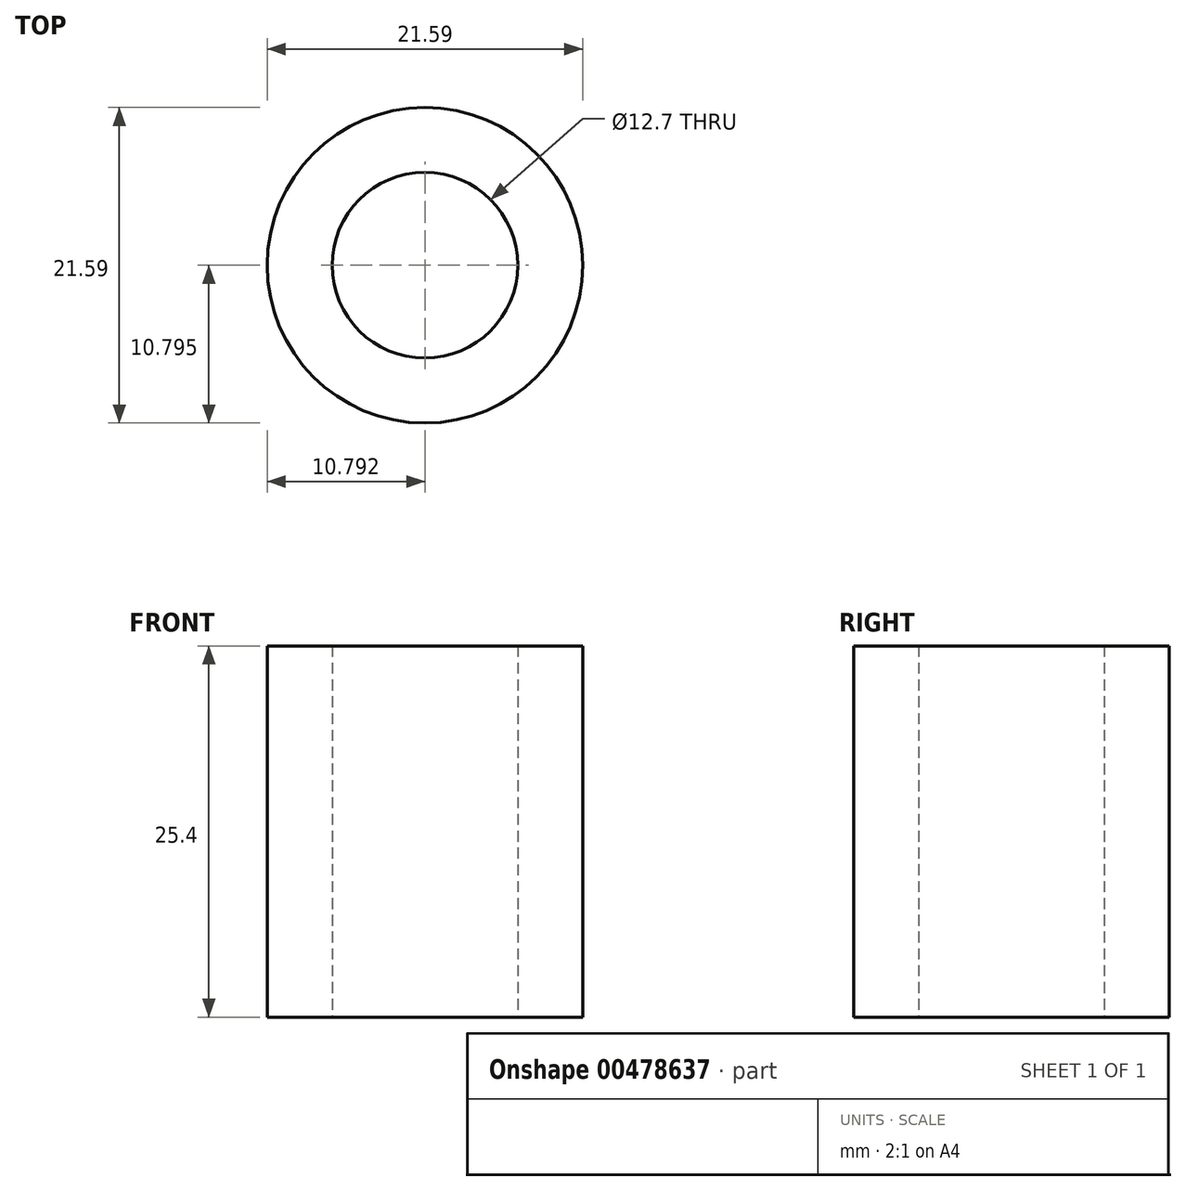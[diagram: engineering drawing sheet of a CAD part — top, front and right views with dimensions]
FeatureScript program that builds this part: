
annotation { "Feature Type Name" : "Feature", "Feature Type Description" : "" }
export const myFeature = defineFeature(function(context is Context, id is Id, definition is map)
    precondition{}
    {
        {
            var Q0;
            Q0=qCreatedBy(makeId("Top.planeOp"),FACE);
            var sketch = newSketch(context, id + "F0", { "sketchPlane" : qUnion([Q0])});
            skCircle(sketch, "E0", {"center": v(-7.67, 25.23) * mm, "radius": 10.8 * mm});
            skCircle(sketch, "E1", {"center": v(-7.67, 25.23) * mm, "radius": 6.35 * mm});
            skSolve(sketch);
        }
        {
            var Q0;
            Q0=makeQuery(id+"F0.imprint","IMPRINT",FACE,{"disambiguationData":[TD([[makeQuery(id+"F0.imprint","IMPRINT",EDGE,{"derivedFrom":sQuery(id+"F0.wireOp",EDGE,"E0")}),1.0]])]});
            extrude(context, id + "F1", {"entities" : qUnion([Q0]), "depth" : 25.4 * mm, "offsetDistance" : 25.4 * mm});
        }
    });
